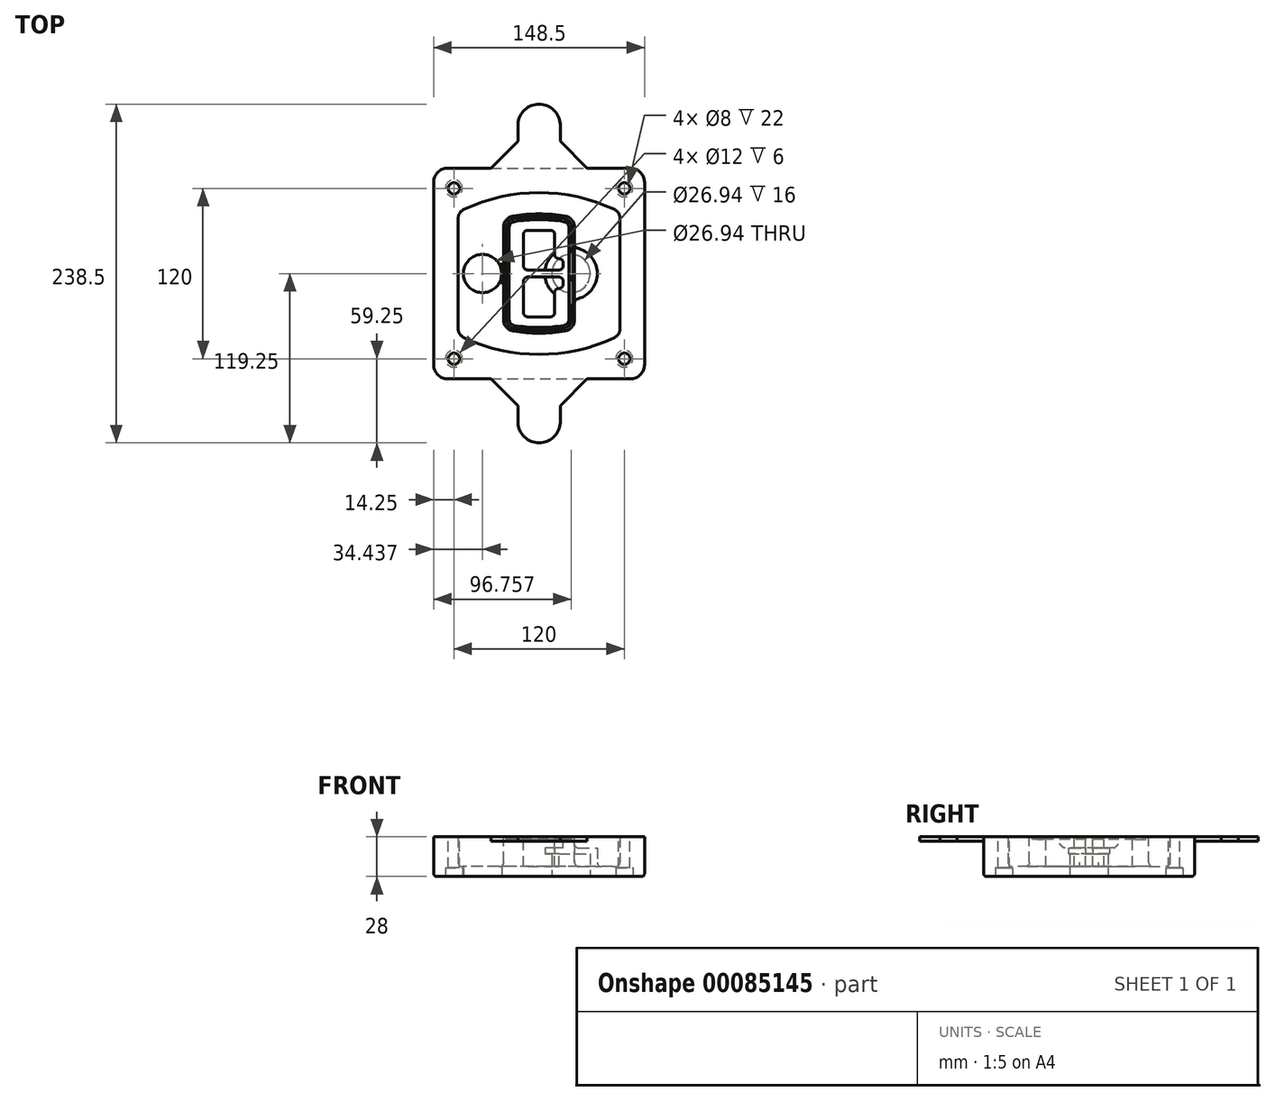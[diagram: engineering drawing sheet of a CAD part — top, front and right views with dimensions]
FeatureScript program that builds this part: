
annotation { "Feature Type Name" : "Feature", "Feature Type Description" : "" }
export const myFeature = defineFeature(function(context is Context, id is Id, definition is map)
    precondition{}
    {
        {
            var Q0;
            Q0=qCreatedBy(makeId("Top.planeOp"),FACE);
            var sketch = newSketch(context, id + "F0", { "sketchPlane" : qUnion([Q0])});
            skPoint(sketch, "E0.rect.middle", {"position": v(0, 0) * mm});
            skLineSegment(sketch, "E1.bottom", {"start": v(-64.25, -74.25) * mm, "end": v(64.25, -74.25) * mm});
            skLineSegment(sketch, "E1.top", {"start": v(-64.25, 74.25) * mm, "end": v(64.25, 74.25) * mm});
            skLineSegment(sketch, "E1.left", {"start": v(-74.25, -64.25) * mm, "end": v(-74.25, 64.25) * mm});
            skLineSegment(sketch, "E1.right", {"start": v(74.25, -64.25) * mm, "end": v(74.25, 64.25) * mm});
            skLineSegment(sketch, "E2", {"start": v(-74.25, 74.25) * mm, "end": v(74.25, -74.25) * mm, "construction": true});
            skLineSegment(sketch, "E3", {"start": v(74.25, 74.25) * mm, "end": v(-74.25, -74.25) * mm, "construction": true});
            skCircle(sketch, "E4", {"center": v(-60, 60) * mm, "radius": 4 * mm});
            skCircle(sketch, "E5", {"center": v(60, 60) * mm, "radius": 4 * mm});
            skCircle(sketch, "E6", {"center": v(60, -60) * mm, "radius": 4 * mm});
            skCircle(sketch, "E7", {"center": v(-60, -60) * mm, "radius": 4 * mm});
            skLineSegment(sketch, "E8", {"start": v(-60, 60) * mm, "end": v(60, 60) * mm, "construction": true});
            skLineSegment(sketch, "E9", {"start": v(60, 60) * mm, "end": v(60, -60) * mm, "construction": true});
            skLineSegment(sketch, "E10", {"start": v(60, -60) * mm, "end": v(-60, -60) * mm, "construction": true});
            skLineSegment(sketch, "E11", {"start": v(-60, -60) * mm, "end": v(-60, 60) * mm, "construction": true});
            skLineSegment(sketch, "E12", {"start": v(-60, 38.83) * mm, "end": v(-60, -38.83) * mm});
            skLineSegment(sketch, "E13", {"start": v(60, 38.83) * mm, "end": v(60, -38.83) * mm});
            skArc(sketch, "E14", {"start": v(54.26, 47.88) * mm, "mid": v(0, 60) * mm, "end": v(-54.26, 47.88) * mm});
            skArc(sketch, "E15", {"start": v(-54.26, -47.88) * mm, "mid": v(0, -60) * mm, "end": v(54.26, -47.88) * mm});
            skLineSegment(sketch, "E16", {"start": v(-60, 0) * mm, "end": v(60, 0) * mm, "construction": true});
            skPoint(sketch, "E17.visualSharp", {"position": v(-60, -45) * mm});
            skArc(sketch, "E17.filletArc", {"start": v(-60, -38.83) * mm, "mid": v(-58.44, -44.2) * mm, "end": v(-54.26, -47.88) * mm});
            skPoint(sketch, "E18.visualSharp", {"position": v(-60, 45) * mm});
            skArc(sketch, "E18.filletArc", {"start": v(-54.26, 47.88) * mm, "mid": v(-58.44, 44.2) * mm, "end": v(-60, 38.83) * mm});
            skPoint(sketch, "E19.visualSharp", {"position": v(60, 45) * mm});
            skArc(sketch, "E19.filletArc", {"start": v(60, 38.83) * mm, "mid": v(58.44, 44.2) * mm, "end": v(54.26, 47.88) * mm});
            skPoint(sketch, "E20.visualSharp", {"position": v(60, -45) * mm});
            skArc(sketch, "E20.filletArc", {"start": v(54.26, -47.88) * mm, "mid": v(58.44, -44.2) * mm, "end": v(60, -38.83) * mm});
            skPoint(sketch, "E21.visualSharp", {"position": v(-74.25, 74.25) * mm});
            skArc(sketch, "E21.filletArc", {"start": v(-64.25, 74.25) * mm, "mid": v(-71.32, 71.32) * mm, "end": v(-74.25, 64.25) * mm});
            skPoint(sketch, "E22.visualSharp", {"position": v(74.25, 74.25) * mm});
            skArc(sketch, "E22.filletArc", {"start": v(74.25, 64.25) * mm, "mid": v(71.32, 71.32) * mm, "end": v(64.25, 74.25) * mm});
            skPoint(sketch, "E23.visualSharp", {"position": v(74.25, -74.25) * mm});
            skArc(sketch, "E23.filletArc", {"start": v(64.25, -74.25) * mm, "mid": v(71.32, -71.32) * mm, "end": v(74.25, -64.25) * mm});
            skPoint(sketch, "E24.visualSharp", {"position": v(-74.25, -74.25) * mm});
            skArc(sketch, "E24.filletArc", {"start": v(-74.25, -64.25) * mm, "mid": v(-71.32, -71.32) * mm, "end": v(-64.25, -74.25) * mm});
            skArc(sketch, "E25.0", {"start": v(57, 38.83) * mm, "mid": v(55.9, 42.58) * mm, "end": v(52.98, 45.17) * mm});
            skLineSegment(sketch, "E25.1", {"start": v(57, 38.83) * mm, "end": v(57, -38.83) * mm});
            skArc(sketch, "E25.2", {"start": v(52.98, -45.17) * mm, "mid": v(55.9, -42.58) * mm, "end": v(57, -38.83) * mm});
            skArc(sketch, "E25.3", {"start": v(-52.98, -45.17) * mm, "mid": v(0, -57) * mm, "end": v(52.98, -45.17) * mm});
            skArc(sketch, "E25.4", {"start": v(-57, -38.83) * mm, "mid": v(-55.9, -42.58) * mm, "end": v(-52.98, -45.17) * mm});
            skArc(sketch, "E25.5", {"start": v(52.98, 45.17) * mm, "mid": v(0, 57) * mm, "end": v(-52.98, 45.17) * mm});
            skLineSegment(sketch, "E25.6", {"start": v(-57, 38.83) * mm, "end": v(-57, -38.83) * mm});
            skArc(sketch, "E25.7", {"start": v(-52.98, 45.17) * mm, "mid": v(-55.9, 42.58) * mm, "end": v(-57, 38.83) * mm});
            skArc(sketch, "E26.0", {"start": v(-55.96, 51.5) * mm, "mid": v(-61.82, 46.33) * mm, "end": v(-64, 38.83) * mm});
            skArc(sketch, "E26.1", {"start": v(55.96, 51.5) * mm, "mid": v(0, 64) * mm, "end": v(-55.96, 51.5) * mm});
            skArc(sketch, "E26.2", {"start": v(64, 38.83) * mm, "mid": v(61.82, 46.33) * mm, "end": v(55.96, 51.5) * mm});
            skLineSegment(sketch, "E26.3", {"start": v(64, 38.83) * mm, "end": v(64, -38.83) * mm});
            skArc(sketch, "E26.4", {"start": v(55.96, -51.5) * mm, "mid": v(61.82, -46.33) * mm, "end": v(64, -38.83) * mm});
            skLineSegment(sketch, "E26.5", {"start": v(-64, 38.83) * mm, "end": v(-64, -38.83) * mm});
            skArc(sketch, "E26.6", {"start": v(-55.96, -51.5) * mm, "mid": v(0, -64) * mm, "end": v(55.96, -51.5) * mm});
            skArc(sketch, "E26.7", {"start": v(-64, -38.83) * mm, "mid": v(-61.82, -46.33) * mm, "end": v(-55.96, -51.5) * mm});
            skSolve(sketch);
        }
        {
            var Q0;
            Q0=makeQuery(id+"F0.imprint","IMPRINT",FACE,{"disambiguationData":[TD([[makeQuery(id+"F0.imprint","IMPRINT",EDGE,{"derivedFrom":sQuery(id+"F0.wireOp",EDGE,"E1.bottom")}),1.0]])]});
            var Q1;
            Q1=makeQuery(id+"F0.imprint","IMPRINT",FACE,{"disambiguationData":[TD([[makeQuery(id+"F0.imprint","IMPRINT",EDGE,{"derivedFrom":sQuery(id+"F0.wireOp",EDGE,"E12")}),1.0]])]});
            var Q2;
            Q2=makeQuery(id+"F0.imprint","IMPRINT",FACE,{"disambiguationData":[TD([[makeQuery(id+"F0.imprint","IMPRINT",EDGE,{"derivedFrom":sQuery(id+"F0.wireOp",EDGE,"E25.0")}),1.0]])]});
            var Q3;
            Q3=makeQuery(id+"F0.imprint","IMPRINT",FACE,{"disambiguationData":[TD([[makeQuery(id+"F0.imprint","IMPRINT",EDGE,{"derivedFrom":sQuery(id+"F0.wireOp",EDGE,"E12")}),-1.0]])]});
            extrude(context, id + "F1", {"entities" : qUnion([Q0, Q1, Q2, Q3]), "oppositeDirection" : true, "depth" : 25 * mm});
        }
        {
            var Q0;
            Q0=makeQuery(id+"F0.imprint","IMPRINT",FACE,{"disambiguationData":[TD([[makeQuery(id+"F0.imprint","IMPRINT",EDGE,{"derivedFrom":sQuery(id+"F0.wireOp",EDGE,"E12")}),1.0]])]});
            extrude(context, id + "F2", {"entities" : qUnion([Q0]), "operationType" : NewBodyOperationType.ADD, "depth" : 3 * mm});
        }
        {
            var Q0;
            Q0=makeQuery(id+"F0.imprint","IMPRINT",FACE,{"disambiguationData":[TD([[makeQuery(id+"F0.imprint","IMPRINT",EDGE,{"derivedFrom":sQuery(id+"F0.wireOp",EDGE,"E25.0")}),1.0]])]});
            extrude(context, id + "F3", {"entities" : qUnion([Q0]), "operationType" : NewBodyOperationType.REMOVE, "oppositeDirection" : true, "depth" : 18 * mm});
        }
        {
            var Q0;
            Q0=makeQuery(id+"F2.opExtrude","CAP_FACE",FACE,{"disambiguationData":[OSD([sQuery(id+"F0.wireOp",EDGE,"E12"),sQuery(id+"F0.wireOp",EDGE,"E13"),sQuery(id+"F0.wireOp",EDGE,"E14"),sQuery(id+"F0.wireOp",EDGE,"E15"),sQuery(id+"F0.wireOp",EDGE,"E17.filletArc"),sQuery(id+"F0.wireOp",EDGE,"E18.filletArc"),sQuery(id+"F0.wireOp",EDGE,"E19.filletArc"),sQuery(id+"F0.wireOp",EDGE,"E20.filletArc"),sQuery(id+"F0.wireOp",EDGE,"E25.0"),sQuery(id+"F0.wireOp",EDGE,"E25.1"),sQuery(id+"F0.wireOp",EDGE,"E25.2"),sQuery(id+"F0.wireOp",EDGE,"E25.3"),sQuery(id+"F0.wireOp",EDGE,"E25.4"),sQuery(id+"F0.wireOp",EDGE,"E25.5"),sQuery(id+"F0.wireOp",EDGE,"E25.6"),sQuery(id+"F0.wireOp",EDGE,"E25.7")])],"isStart":false});
            var sketch = newSketch(context, id + "F4", { "sketchPlane" : qUnion([Q0])});
            skArc(sketch, "E27.0", {"start": v(-18.34, -40.45) * mm, "mid": v(0, -42) * mm, "end": v(18.34, -40.45) * mm});
            skArc(sketch, "E28.0", {"start": v(18.34, 40.45) * mm, "mid": v(0, 42) * mm, "end": v(-18.34, 40.45) * mm});
            skLineSegment(sketch, "E29", {"start": v(-25, 32.57) * mm, "end": v(-25, -32.57) * mm});
            skLineSegment(sketch, "E30", {"start": v(25, 32.57) * mm, "end": v(25, -32.57) * mm});
            skLineSegment(sketch, "E31", {"start": v(-25, 39.1) * mm, "end": v(25, 39.1) * mm, "construction": true});
            skLineSegment(sketch, "E32", {"start": v(-25, -39.1) * mm, "end": v(25, -39.1) * mm, "construction": true});
            skPoint(sketch, "E33.visualSharp", {"position": v(-25, 39.1) * mm});
            skArc(sketch, "E33.filletArc", {"start": v(-18.34, 40.45) * mm, "mid": v(-23.11, 37.73) * mm, "end": v(-25, 32.57) * mm});
            skPoint(sketch, "E34.visualSharp", {"position": v(25, 39.1) * mm});
            skArc(sketch, "E34.filletArc", {"start": v(25, 32.57) * mm, "mid": v(23.11, 37.73) * mm, "end": v(18.34, 40.45) * mm});
            skPoint(sketch, "E35.visualSharp", {"position": v(25, -39.1) * mm});
            skArc(sketch, "E35.filletArc", {"start": v(18.34, -40.45) * mm, "mid": v(23.11, -37.73) * mm, "end": v(25, -32.57) * mm});
            skPoint(sketch, "E36.visualSharp", {"position": v(-25, -39.1) * mm});
            skArc(sketch, "E36.filletArc", {"start": v(-25, -32.57) * mm, "mid": v(-23.11, -37.73) * mm, "end": v(-18.34, -40.45) * mm});
            skArc(sketch, "E37.0", {"start": v(52.98, 45.17) * mm, "mid": v(0, 57) * mm, "end": v(-52.98, 45.17) * mm});
            skArc(sketch, "E37.1", {"start": v(-52.98, 45.17) * mm, "mid": v(-55.9, 42.58) * mm, "end": v(-57, 38.83) * mm});
            skLineSegment(sketch, "E37.2", {"start": v(-57, 38.83) * mm, "end": v(-57, -38.83) * mm});
            skArc(sketch, "E37.3", {"start": v(-57, -38.83) * mm, "mid": v(-55.9, -42.58) * mm, "end": v(-52.98, -45.17) * mm});
            skArc(sketch, "E37.4", {"start": v(-52.98, -45.17) * mm, "mid": v(0, -57) * mm, "end": v(52.98, -45.17) * mm});
            skArc(sketch, "E37.5", {"start": v(52.98, -45.17) * mm, "mid": v(55.9, -42.58) * mm, "end": v(57, -38.83) * mm});
            skLineSegment(sketch, "E37.6", {"start": v(57, 38.83) * mm, "end": v(57, -38.83) * mm});
            skArc(sketch, "E37.7", {"start": v(57, 38.83) * mm, "mid": v(55.9, 42.58) * mm, "end": v(52.98, 45.17) * mm});
            skLineSegment(sketch, "E38.0", {"start": v(23, 32.57) * mm, "end": v(23, -32.57) * mm});
            skArc(sketch, "E38.1", {"start": v(18, -38.48) * mm, "mid": v(21.58, -36.44) * mm, "end": v(23, -32.57) * mm});
            skArc(sketch, "E38.2", {"start": v(-18, -38.48) * mm, "mid": v(0, -40) * mm, "end": v(18, -38.48) * mm});
            skArc(sketch, "E38.3", {"start": v(-23, -32.57) * mm, "mid": v(-21.58, -36.44) * mm, "end": v(-18, -38.48) * mm});
            skLineSegment(sketch, "E38.4", {"start": v(-23, 32.57) * mm, "end": v(-23, -32.57) * mm});
            skArc(sketch, "E38.5", {"start": v(23, 32.57) * mm, "mid": v(21.58, 36.44) * mm, "end": v(18, 38.48) * mm});
            skArc(sketch, "E38.6", {"start": v(-18, 38.48) * mm, "mid": v(-21.58, 36.44) * mm, "end": v(-23, 32.57) * mm});
            skArc(sketch, "E38.7", {"start": v(18, 38.48) * mm, "mid": v(0, 40) * mm, "end": v(-18, 38.48) * mm});
            skArc(sketch, "E39.0", {"start": v(21, 32.57) * mm, "mid": v(20.06, 35.15) * mm, "end": v(17.67, 36.5) * mm});
            skLineSegment(sketch, "E39.1", {"start": v(21, 32.57) * mm, "end": v(21, -32.57) * mm});
            skArc(sketch, "E39.2", {"start": v(17.67, -36.5) * mm, "mid": v(20.06, -35.15) * mm, "end": v(21, -32.57) * mm});
            skArc(sketch, "E39.3", {"start": v(-17.67, -36.5) * mm, "mid": v(0, -38) * mm, "end": v(17.67, -36.5) * mm});
            skArc(sketch, "E39.4", {"start": v(-21, -32.57) * mm, "mid": v(-20.06, -35.15) * mm, "end": v(-17.67, -36.5) * mm});
            skArc(sketch, "E39.5", {"start": v(17.67, 36.5) * mm, "mid": v(0, 38) * mm, "end": v(-17.67, 36.5) * mm});
            skLineSegment(sketch, "E39.6", {"start": v(-21, 32.57) * mm, "end": v(-21, -32.57) * mm});
            skArc(sketch, "E39.7", {"start": v(-17.67, 36.5) * mm, "mid": v(-20.06, 35.15) * mm, "end": v(-21, 32.57) * mm});
            skLineSegment(sketch, "E40", {"start": v(-25, 0) * mm, "end": v(25, 0) * mm, "construction": true});
            skLineSegment(sketch, "E41", {"start": v(-11, 5.5) * mm, "end": v(-11, 27.5) * mm});
            skLineSegment(sketch, "E42", {"start": v(-8, 30.5) * mm, "end": v(8, 30.5) * mm});
            skLineSegment(sketch, "E43", {"start": v(11, 27.5) * mm, "end": v(11, 13.5) * mm});
            skLineSegment(sketch, "E44", {"start": v(14, 10.5) * mm, "end": v(14, 10.5) * mm});
            skLineSegment(sketch, "E45", {"start": v(17, 7.5) * mm, "end": v(17, 5.5) * mm});
            skLineSegment(sketch, "E46", {"start": v(14, 2.5) * mm, "end": v(-8, 2.5) * mm});
            skPoint(sketch, "E47.visualSharp", {"position": v(-11, 30.5) * mm});
            skArc(sketch, "E47.filletArc", {"start": v(-8, 30.5) * mm, "mid": v(-10.12, 29.62) * mm, "end": v(-11, 27.5) * mm});
            skPoint(sketch, "E48.visualSharp", {"position": v(11, 30.5) * mm});
            skArc(sketch, "E48.filletArc", {"start": v(11, 27.5) * mm, "mid": v(10.12, 29.62) * mm, "end": v(8, 30.5) * mm});
            skPoint(sketch, "E49.visualSharp", {"position": v(11, 10.5) * mm});
            skArc(sketch, "E49.filletArc", {"start": v(11, 13.5) * mm, "mid": v(11.88, 11.38) * mm, "end": v(14, 10.5) * mm});
            skPoint(sketch, "E50.visualSharp", {"position": v(17, 10.5) * mm});
            skArc(sketch, "E50.filletArc", {"start": v(17, 7.5) * mm, "mid": v(16.12, 9.62) * mm, "end": v(14, 10.5) * mm});
            skPoint(sketch, "E51.visualSharp", {"position": v(17, 2.5) * mm});
            skArc(sketch, "E51.filletArc", {"start": v(14, 2.5) * mm, "mid": v(16.12, 3.38) * mm, "end": v(17, 5.5) * mm});
            skPoint(sketch, "E52.visualSharp", {"position": v(-11, 2.5) * mm});
            skArc(sketch, "E52.filletArc", {"start": v(-11, 5.5) * mm, "mid": v(-10.12, 3.38) * mm, "end": v(-8, 2.5) * mm});
            skLineSegment(sketch, "E53.0.MirrorCS", {"start": v(14, -2.5) * mm, "end": v(-8, -2.5) * mm});
            skArc(sketch, "E54.0.MirrorCS", {"start": v(-11, -5.5) * mm, "mid": v(-10.12, -3.38) * mm, "end": v(-8, -2.5) * mm});
            skLineSegment(sketch, "E55.0.MirrorCS", {"start": v(-11, -5.5) * mm, "end": v(-11, -27.5) * mm});
            skArc(sketch, "E56.0.MirrorCS", {"start": v(-8, -30.5) * mm, "mid": v(-10.12, -29.62) * mm, "end": v(-11, -27.5) * mm});
            skLineSegment(sketch, "E57.0.MirrorCS", {"start": v(-8, -30.5) * mm, "end": v(8, -30.5) * mm});
            skArc(sketch, "E58.0.MirrorCS", {"start": v(11, -27.5) * mm, "mid": v(10.12, -29.62) * mm, "end": v(8, -30.5) * mm});
            skLineSegment(sketch, "E59.0.MirrorCS", {"start": v(11, -27.5) * mm, "end": v(11, -13.5) * mm});
            skArc(sketch, "E60.0.MirrorCS", {"start": v(11, -13.5) * mm, "mid": v(11.88, -11.38) * mm, "end": v(14, -10.5) * mm});
            skArc(sketch, "E61.0.MirrorCS", {"start": v(17, -7.5) * mm, "mid": v(16.12, -9.62) * mm, "end": v(14, -10.5) * mm});
            skLineSegment(sketch, "E62.0.MirrorCS", {"start": v(17, -7.5) * mm, "end": v(17, -5.5) * mm});
            skArc(sketch, "E63.0.MirrorCS", {"start": v(14, -2.5) * mm, "mid": v(16.12, -3.38) * mm, "end": v(17, -5.5) * mm});
            skSolve(sketch);
        }
        {
            var Q0;
            Q0=makeQuery(id+"F4.imprint","IMPRINT",FACE,{"disambiguationData":[TD([[makeQuery(id+"F4.imprint","IMPRINT",EDGE,{"derivedFrom":sQuery(id+"F4.wireOp",EDGE,"E27.0")}),1.0]])]});
            var Q1;
            Q1=makeQuery(id+"F4.imprint","IMPRINT",FACE,{"disambiguationData":[TD([[makeQuery(id+"F4.imprint","IMPRINT",EDGE,{"derivedFrom":sQuery(id+"F4.wireOp",EDGE,"E38.0")}),-1.0]])]});
            var Q2;
            Q2=makeQuery(id+"F4.imprint","IMPRINT",FACE,{"disambiguationData":[TD([[makeQuery(id+"F4.imprint","IMPRINT",EDGE,{"derivedFrom":sQuery(id+"F4.wireOp",EDGE,"E39.0")}),1.0]])]});
            extrude(context, id + "F5", {"entities" : qUnion([Q0, Q1, Q2]), "operationType" : NewBodyOperationType.ADD, "endBound" : BoundingType.UP_TO_NEXT, "oppositeDirection" : true, "depth" : 25 * mm});
        }
        {
            var Q0;
            Q0=makeQuery(id+"F4.imprint","IMPRINT",FACE,{"disambiguationData":[TD([[makeQuery(id+"F4.imprint","IMPRINT",EDGE,{"derivedFrom":sQuery(id+"F4.wireOp",EDGE,"E38.0")}),-1.0]])]});
            extrude(context, id + "F6", {"entities" : qUnion([Q0]), "operationType" : NewBodyOperationType.REMOVE, "oppositeDirection" : true, "depth" : 2 * mm});
        }
        {
            var Q0;
            Q0=makeQuery(id+"F1.opExtrude","CAP_FACE",FACE,{"disambiguationData":[OSD([sQuery(id+"F0.wireOp",EDGE,"E1.bottom"),sQuery(id+"F0.wireOp",EDGE,"E1.top"),sQuery(id+"F0.wireOp",EDGE,"E1.left"),sQuery(id+"F0.wireOp",EDGE,"E1.right"),sQuery(id+"F0.wireOp",EDGE,"E4"),sQuery(id+"F0.wireOp",EDGE,"E5"),sQuery(id+"F0.wireOp",EDGE,"E6"),sQuery(id+"F0.wireOp",EDGE,"E7"),sQuery(id+"F0.wireOp",EDGE,"E21.filletArc"),sQuery(id+"F0.wireOp",EDGE,"E22.filletArc"),sQuery(id+"F0.wireOp",EDGE,"E23.filletArc"),sQuery(id+"F0.wireOp",EDGE,"E24.filletArc")])],"isStart":false});
            var sketch = newSketch(context, id + "F7", { "sketchPlane" : qUnion([Q0])});
            skCircle(sketch, "E64", {"center": v(22.5, 0) * mm, "radius": 13.47 * mm});
            skCircle(sketch, "E65", {"center": v(-39.81, 0) * mm, "radius": 13.47 * mm});
            skLineSegment(sketch, "E66", {"start": v(74.25, 0) * mm, "end": v(-74.25, 0) * mm});
            skCircle(sketch, "E67", {"center": v(22.5, 0) * mm, "radius": 18.47 * mm});
            skCircle(sketch, "E68", {"center": v(60, -60) * mm, "radius": 6 * mm});
            skCircle(sketch, "E69", {"center": v(-60, -60) * mm, "radius": 6 * mm});
            skCircle(sketch, "E70", {"center": v(-60, 60) * mm, "radius": 6 * mm});
            skCircle(sketch, "E71", {"center": v(60, 60) * mm, "radius": 6 * mm});
            skSolve(sketch);
        }
        {
            var Q0;
            {var subQ1=sQuery(id+"F7.wireOp",EDGE,"E66");var subQ4=sQuery(id+"F7.wireOp",EDGE,"E64");var subQ6=makeQuery(id+"F7.imprint","INTERSECT",VERTEX,{"disambiguationData":[OD(0.0)],"derivedFrom":[subQ4,subQ1]});Q0=makeQuery(id+"F7.imprint","IMPRINT",FACE,{"disambiguationData":[TD([[makeQuery(id+"F7.imprint","IMPRINT",EDGE,{"disambiguationData":[TD([[subQ6,-1.0]])],"derivedFrom":subQ4}),-1.0]])]});}
            var Q1;
            {var subQ0=sQuery(id+"F7.wireOp",EDGE,"E66");var subQ1=sQuery(id+"F7.wireOp",EDGE,"E64");var subQ3=makeQuery(id+"F7.imprint","INTERSECT",VERTEX,{"disambiguationData":[OD(0.0)],"derivedFrom":[subQ1,subQ0]});Q1=makeQuery(id+"F7.imprint","IMPRINT",FACE,{"disambiguationData":[TD([[makeQuery(id+"F7.imprint","IMPRINT",EDGE,{"disambiguationData":[TD([[subQ3,-1.0]])],"derivedFrom":subQ1}),1.0]])]});}
            var Q2;
            {var subQ0=sQuery(id+"F7.wireOp",EDGE,"E66");var subQ1=sQuery(id+"F7.wireOp",EDGE,"E64");var subQ3=makeQuery(id+"F7.imprint","INTERSECT",VERTEX,{"disambiguationData":[OD(0.0)],"derivedFrom":[subQ1,subQ0]});Q2=makeQuery(id+"F7.imprint","IMPRINT",FACE,{"disambiguationData":[TD([[makeQuery(id+"F7.imprint","IMPRINT",EDGE,{"disambiguationData":[TD([[subQ3,1.0]])],"derivedFrom":subQ1}),1.0]])]});}
            var Q3;
            {var subQ1=sQuery(id+"F7.wireOp",EDGE,"E66");var subQ4=sQuery(id+"F7.wireOp",EDGE,"E64");var subQ6=makeQuery(id+"F7.imprint","INTERSECT",VERTEX,{"disambiguationData":[OD(0.0)],"derivedFrom":[subQ4,subQ1]});Q3=makeQuery(id+"F7.imprint","IMPRINT",FACE,{"disambiguationData":[TD([[makeQuery(id+"F7.imprint","IMPRINT",EDGE,{"disambiguationData":[TD([[subQ6,1.0]])],"derivedFrom":subQ4}),-1.0]])]});}
            extrude(context, id + "F8", {"entities" : qUnion([Q0, Q1, Q2, Q3]), "operationType" : NewBodyOperationType.ADD, "oppositeDirection" : true, "depth" : 20 * mm});
        }
        {
            var Q0;
            {var subQ0=sQuery(id+"F7.wireOp",EDGE,"E66");var subQ1=sQuery(id+"F7.wireOp",EDGE,"E64");var subQ3=makeQuery(id+"F7.imprint","INTERSECT",VERTEX,{"disambiguationData":[OD(0.0)],"derivedFrom":[subQ1,subQ0]});Q0=makeQuery(id+"F7.imprint","IMPRINT",FACE,{"disambiguationData":[TD([[makeQuery(id+"F7.imprint","IMPRINT",EDGE,{"disambiguationData":[TD([[subQ3,-1.0]])],"derivedFrom":subQ1}),1.0]])]});}
            var Q1;
            {var subQ0=sQuery(id+"F7.wireOp",EDGE,"E66");var subQ1=sQuery(id+"F7.wireOp",EDGE,"E64");var subQ3=makeQuery(id+"F7.imprint","INTERSECT",VERTEX,{"disambiguationData":[OD(0.0)],"derivedFrom":[subQ1,subQ0]});Q1=makeQuery(id+"F7.imprint","IMPRINT",FACE,{"disambiguationData":[TD([[makeQuery(id+"F7.imprint","IMPRINT",EDGE,{"disambiguationData":[TD([[subQ3,1.0]])],"derivedFrom":subQ1}),1.0]])]});}
            extrude(context, id + "F9", {"entities" : qUnion([Q0, Q1]), "operationType" : NewBodyOperationType.REMOVE, "oppositeDirection" : true, "depth" : 16 * mm});
        }
        {
            var Q0;
            {var subQ0=sQuery(id+"F7.wireOp",EDGE,"E66");var subQ1=sQuery(id+"F7.wireOp",EDGE,"E65");var subQ3=makeQuery(id+"F7.imprint","INTERSECT",VERTEX,{"disambiguationData":[OD(0.0)],"derivedFrom":[subQ1,subQ0]});Q0=makeQuery(id+"F7.imprint","IMPRINT",FACE,{"disambiguationData":[TD([[makeQuery(id+"F7.imprint","IMPRINT",EDGE,{"disambiguationData":[TD([[subQ3,-1.0]])],"derivedFrom":subQ1}),1.0]])]});}
            var Q1;
            {var subQ0=sQuery(id+"F7.wireOp",EDGE,"E66");var subQ1=sQuery(id+"F7.wireOp",EDGE,"E65");var subQ3=makeQuery(id+"F7.imprint","INTERSECT",VERTEX,{"disambiguationData":[OD(0.0)],"derivedFrom":[subQ1,subQ0]});Q1=makeQuery(id+"F7.imprint","IMPRINT",FACE,{"disambiguationData":[TD([[makeQuery(id+"F7.imprint","IMPRINT",EDGE,{"disambiguationData":[TD([[subQ3,1.0]])],"derivedFrom":subQ1}),1.0]])]});}
            extrude(context, id + "F10", {"entities" : qUnion([Q0, Q1]), "operationType" : NewBodyOperationType.REMOVE, "oppositeDirection" : true, "depth" : 25 * mm});
        }
        {
            var Q0;
            Q0=makeQuery(id+"F7.imprint","IMPRINT",FACE,{"disambiguationData":[TD([[makeQuery(id+"F7.imprint","IMPRINT",EDGE,{"derivedFrom":sQuery(id+"F7.wireOp",EDGE,"E68")}),1.0]])]});
            var Q1;
            Q1=makeQuery(id+"F7.imprint","IMPRINT",FACE,{"disambiguationData":[TD([[makeQuery(id+"F7.imprint","IMPRINT",EDGE,{"derivedFrom":makeQuery(id+"F1.opExtrude","CAP_EDGE",EDGE,{"disambiguationData":[OSD([sQuery(id+"F0.wireOp",EDGE,"E5")])],"isStart":false})}),-1.0]])]});
            var Q2;
            Q2=makeQuery(id+"F7.imprint","IMPRINT",FACE,{"disambiguationData":[TD([[makeQuery(id+"F7.imprint","IMPRINT",EDGE,{"derivedFrom":sQuery(id+"F7.wireOp",EDGE,"E69")}),1.0]])]});
            var Q3;
            Q3=makeQuery(id+"F7.imprint","IMPRINT",FACE,{"disambiguationData":[TD([[makeQuery(id+"F7.imprint","IMPRINT",EDGE,{"derivedFrom":makeQuery(id+"F1.opExtrude","CAP_EDGE",EDGE,{"disambiguationData":[OSD([sQuery(id+"F0.wireOp",EDGE,"E4")])],"isStart":false})}),-1.0]])]});
            var Q4;
            Q4=makeQuery(id+"F7.imprint","IMPRINT",FACE,{"disambiguationData":[TD([[makeQuery(id+"F7.imprint","IMPRINT",EDGE,{"derivedFrom":sQuery(id+"F7.wireOp",EDGE,"E70")}),1.0]])]});
            var Q5;
            Q5=makeQuery(id+"F7.imprint","IMPRINT",FACE,{"disambiguationData":[TD([[makeQuery(id+"F7.imprint","IMPRINT",EDGE,{"derivedFrom":makeQuery(id+"F1.opExtrude","CAP_EDGE",EDGE,{"disambiguationData":[OSD([sQuery(id+"F0.wireOp",EDGE,"E7")])],"isStart":false})}),-1.0]])]});
            var Q6;
            Q6=makeQuery(id+"F7.imprint","IMPRINT",FACE,{"disambiguationData":[TD([[makeQuery(id+"F7.imprint","IMPRINT",EDGE,{"derivedFrom":sQuery(id+"F7.wireOp",EDGE,"E71")}),1.0]])]});
            var Q7;
            Q7=makeQuery(id+"F7.imprint","IMPRINT",FACE,{"disambiguationData":[TD([[makeQuery(id+"F7.imprint","IMPRINT",EDGE,{"derivedFrom":makeQuery(id+"F1.opExtrude","CAP_EDGE",EDGE,{"disambiguationData":[OSD([sQuery(id+"F0.wireOp",EDGE,"E6")])],"isStart":false})}),-1.0]])]});
            extrude(context, id + "F11", {"entities" : qUnion([Q0, Q1, Q2, Q3, Q4, Q5, Q6, Q7]), "operationType" : NewBodyOperationType.REMOVE, "oppositeDirection" : true, "depth" : 6 * mm});
        }
        {
            var Q0;
            Q0=makeQuery(id+"F9.boolean.opBoolean","COPY",FACE,{"derivedFrom":makeQuery(id+"F9.opExtrude","CAP_FACE",FACE,{"disambiguationData":[OSD([sQuery(id+"F7.wireOp",EDGE,"E64")])],"isStart":false})});
            var sketch = newSketch(context, id + "F12", { "sketchPlane" : qUnion([Q0])});
            skArc(sketch, "E72.0", {"start": v(11, 14.45) * mm, "mid": v(6.45, 9.13) * mm, "end": v(4.2, 2.5) * mm});
            skArc(sketch, "E72.1", {"start": v(4.2, -2.5) * mm, "mid": v(6.45, -9.13) * mm, "end": v(11, -14.45) * mm});
            skLineSegment(sketch, "E73", {"start": v(4.2, -2.5) * mm, "end": v(14, -2.5) * mm});
            skLineSegment(sketch, "E74.0", {"start": v(14, 2.5) * mm, "end": v(4.2, 2.5) * mm});
            skArc(sketch, "E74.1", {"start": v(14, 2.5) * mm, "mid": v(16.12, 3.38) * mm, "end": v(17, 5.5) * mm});
            skLineSegment(sketch, "E74.2", {"start": v(17, 7.5) * mm, "end": v(17, 5.5) * mm});
            skArc(sketch, "E74.3", {"start": v(17, 7.5) * mm, "mid": v(16.12, 9.62) * mm, "end": v(14, 10.5) * mm});
            skArc(sketch, "E74.4", {"start": v(11, 13.5) * mm, "mid": v(11.88, 11.38) * mm, "end": v(14, 10.5) * mm});
            skLineSegment(sketch, "E74.5", {"start": v(11, 14.45) * mm, "end": v(11, 13.5) * mm});
            skLineSegment(sketch, "E74.7", {"start": v(14, -2.5) * mm, "end": v(4.2, -2.5) * mm});
            skArc(sketch, "E74.8", {"start": v(14, -2.5) * mm, "mid": v(16.12, -3.38) * mm, "end": v(17, -5.5) * mm});
            skLineSegment(sketch, "E74.9", {"start": v(17, -7.5) * mm, "end": v(17, -5.5) * mm});
            skArc(sketch, "E74.10", {"start": v(17, -7.5) * mm, "mid": v(16.12, -9.62) * mm, "end": v(14, -10.5) * mm});
            skArc(sketch, "E74.11", {"start": v(11, -13.5) * mm, "mid": v(11.88, -11.38) * mm, "end": v(14, -10.5) * mm});
            skLineSegment(sketch, "E74.12", {"start": v(11, -14.45) * mm, "end": v(11, -13.5) * mm});
            skPoint(sketch, "E75.orphan", {"position": v(11, -27.5) * mm});
            skPoint(sketch, "E76.orphan", {"position": v(-8, -2.5) * mm});
            skPoint(sketch, "E77.orphan", {"position": v(-8, 2.5) * mm});
            skPoint(sketch, "E78.orphan", {"position": v(11, 27.5) * mm});
            skSolve(sketch);
        }
        {
            var Q0;
            {var subQ7=sQuery(id+"F12.wireOp",EDGE,"E72.0");var subQ14=sQuery(id+"F12.wireOp",EDGE,"E72.1");var subQ16=sQuery(id+"F12.wireOp",EDGE,"E74.1");var subQ18=sQuery(id+"F12.wireOp",EDGE,"E74.8");Q0=qUnion([makeQuery(id+"F12.imprint","IMPRINT",FACE,{"disambiguationData":[TD([[makeQuery(id+"F12.imprint","IMPRINT",EDGE,{"derivedFrom":subQ7}),1.0]])]}),makeQuery(id+"F12.imprint","IMPRINT",FACE,{"disambiguationData":[TD([[makeQuery(id+"F12.imprint","IMPRINT",EDGE,{"derivedFrom":subQ14}),1.0]])]}),makeQuery(id+"F12.imprint","IMPRINT",FACE,{"disambiguationData":[TD([[makeQuery(id+"F12.imprint","IMPRINT",EDGE,{"derivedFrom":subQ16}),1.0]])]}),makeQuery(id+"F12.imprint","IMPRINT",FACE,{"disambiguationData":[TD([[makeQuery(id+"F12.imprint","IMPRINT",EDGE,{"derivedFrom":subQ18}),-1.0]])]})]);}
            var Q1;
            Q1=makeQuery(id+"F5.boolean.opBoolean","SPLIT",FACE,{"disambiguationData":[TD([makeQuery(id+"F5.opExtrude","SWEPT_FACE",FACE,{"disambiguationData":[OSD([sQuery(id+"F4.wireOp",EDGE,"E41")])]})])],"derivedFrom":makeQuery(id+"F3.boolean.opBoolean","COPY",FACE,{"derivedFrom":makeQuery(id+"F3.opExtrude","CAP_FACE",FACE,{"disambiguationData":[OSD([sQuery(id+"F0.wireOp",EDGE,"E25.0"),sQuery(id+"F0.wireOp",EDGE,"E25.1"),sQuery(id+"F0.wireOp",EDGE,"E25.2"),sQuery(id+"F0.wireOp",EDGE,"E25.3"),sQuery(id+"F0.wireOp",EDGE,"E25.4"),sQuery(id+"F0.wireOp",EDGE,"E25.5"),sQuery(id+"F0.wireOp",EDGE,"E25.6"),sQuery(id+"F0.wireOp",EDGE,"E25.7")])],"isStart":false})})});
            extrude(context, id + "F13", {"entities" : qUnion([Q0]), "operationType" : NewBodyOperationType.REMOVE, "endBound" : BoundingType.UP_TO_SURFACE, "endBoundEntityFace" : qUnion([Q1]), "depth" : 25 * mm});
        }
        {
            var Q0;
            Q0=makeQuery(id+"F3.boolean.opBoolean","COPY",EDGE,{"derivedFrom":makeQuery(id+"F3.opExtrude","CAP_EDGE",EDGE,{"disambiguationData":[OSD([sQuery(id+"F0.wireOp",EDGE,"E25.6")])],"isStart":false})});
            var Q1;
            Q1=makeQuery(id+"F8.boolean.opBoolean","INTERSECT",EDGE,{"derivedFrom":[makeQuery(id+"F5.opExtrude","SWEPT_FACE",FACE,{"disambiguationData":[OSD([sQuery(id+"F4.wireOp",EDGE,"E30")])]}),makeQuery(id+"F8.opExtrude","CAP_FACE",FACE,{"disambiguationData":[OSD([sQuery(id+"F7.wireOp",EDGE,"E67")])],"isStart":false})]});
            var Q2;
            Q2=makeQuery(id+"F8.boolean.opBoolean","INTERSECT",EDGE,{"disambiguationData":[OD(1.0)],"derivedFrom":[makeQuery(id+"F5.opExtrude","SWEPT_FACE",FACE,{"disambiguationData":[OSD([sQuery(id+"F4.wireOp",EDGE,"E30")])]}),makeQuery(id+"F8.opExtrude","SWEPT_FACE",FACE,{"disambiguationData":[OSD([sQuery(id+"F7.wireOp",EDGE,"E67")])]})]});
            var Q3;
            {var subQ0=sQuery(id+"F4.wireOp",EDGE,"E30");Q3=makeQuery(id+"F8.boolean.opBoolean","SPLIT",EDGE,{"disambiguationData":[TD([makeQuery(id+"F5.opExtrude","SWEPT_FACE",FACE,{"disambiguationData":[OSD([sQuery(id+"F4.wireOp",EDGE,"E35.filletArc")])]})])],"derivedFrom":makeQuery(id+"F5.opExtrude","CAP_EDGE",EDGE,{"disambiguationData":[OSD([subQ0])],"isStart":false})});}
            var Q4;
            {var subQ0=sQuery(id+"F0.wireOp",EDGE,"E25.7");var subQ1=sQuery(id+"F0.wireOp",EDGE,"E25.1");var subQ2=sQuery(id+"F0.wireOp",EDGE,"E25.6");var subQ3=sQuery(id+"F0.wireOp",EDGE,"E25.5");var subQ4=sQuery(id+"F0.wireOp",EDGE,"E25.4");var subQ5=sQuery(id+"F0.wireOp",EDGE,"E25.0");var subQ6=sQuery(id+"F0.wireOp",EDGE,"E25.2");var subQ7=sQuery(id+"F0.wireOp",EDGE,"E25.3");Q4=makeQuery(id+"F8.boolean.opBoolean","INTERSECT",EDGE,{"derivedFrom":[makeQuery(id+"F5.boolean.opBoolean","SPLIT",FACE,{"disambiguationData":[TD([makeQuery(id+"F2.opExtrude","SWEPT_FACE",FACE,{"disambiguationData":[OSD([subQ5])]})])],"derivedFrom":makeQuery(id+"F3.boolean.opBoolean","COPY",FACE,{"derivedFrom":makeQuery(id+"F3.opExtrude","CAP_FACE",FACE,{"disambiguationData":[OSD([subQ5,subQ1,subQ6,subQ7,subQ4,subQ3,subQ2,subQ0])],"isStart":false})})}),makeQuery(id+"F8.opExtrude","SWEPT_FACE",FACE,{"disambiguationData":[OSD([sQuery(id+"F7.wireOp",EDGE,"E67")])]})]});}
            var Q5;
            Q5=makeQuery(id+"F8.boolean.opBoolean","INTERSECT",EDGE,{"disambiguationData":[OD(0.0)],"derivedFrom":[makeQuery(id+"F5.opExtrude","SWEPT_FACE",FACE,{"disambiguationData":[OSD([sQuery(id+"F4.wireOp",EDGE,"E30")])]}),makeQuery(id+"F8.opExtrude","SWEPT_FACE",FACE,{"disambiguationData":[OSD([sQuery(id+"F7.wireOp",EDGE,"E67")])]})]});
            fillet(context, id + "F14", {"entities" : qUnion([Q0, Q1, Q2, Q3, Q4, Q5]), "radius" : 3 * mm, "tangentPropagation" : true, "allowEdgeOverflow" : false});
        }
        {
            var Q0;
            Q0=makeQuery(id+"F1.opExtrude","CAP_EDGE",EDGE,{"disambiguationData":[OSD([sQuery(id+"F0.wireOp",EDGE,"E1.bottom")])],"isStart":false});
            fillet(context, id + "F15", {"entities" : qUnion([Q0]), "radius" : 2 * mm, "tangentPropagation" : true, "allowEdgeOverflow" : false});
        }
        {
            var Q0;
            {var subQ0=sQuery(id+"F0.wireOp",EDGE,"E22.filletArc");var subQ1=sQuery(id+"F0.wireOp",EDGE,"E7");var subQ2=sQuery(id+"F0.wireOp",EDGE,"E6");var subQ3=sQuery(id+"F0.wireOp",EDGE,"E5");var subQ4=sQuery(id+"F0.wireOp",EDGE,"E4");var subQ5=sQuery(id+"F0.wireOp",EDGE,"E1.bottom");var subQ6=sQuery(id+"F0.wireOp",EDGE,"E21.filletArc");var subQ7=sQuery(id+"F0.wireOp",EDGE,"E1.top");var subQ8=sQuery(id+"F0.wireOp",EDGE,"E1.left");var subQ9=sQuery(id+"F0.wireOp",EDGE,"E1.right");var subQ10=sQuery(id+"F0.wireOp",EDGE,"E23.filletArc");var subQ11=sQuery(id+"F0.wireOp",EDGE,"E24.filletArc");Q0=makeQuery(id+"F2.boolean.opBoolean","SPLIT",FACE,{"disambiguationData":[TD([makeQuery(id+"F1.opExtrude","SWEPT_FACE",FACE,{"disambiguationData":[OSD([subQ5])]})])],"derivedFrom":makeQuery(id+"F1.opExtrude","CAP_FACE",FACE,{"disambiguationData":[OSD([subQ5,subQ7,subQ8,subQ9,subQ4,subQ3,subQ2,subQ1,subQ6,subQ0,subQ10,subQ11])],"isStart":true})});}
            var sketch = newSketch(context, id + "F16", { "sketchPlane" : qUnion([Q0])});
            skLineSegment(sketch, "E79", {"start": v(0, 74.25) * mm, "end": v(0, 104.25) * mm, "construction": true});
            skCircle(sketch, "E80", {"center": v(0, 104.25) * mm, "radius": 6 * mm});
            skArc(sketch, "E81", {"start": v(14.98, 105.1) * mm, "mid": v(0.03, 119.25) * mm, "end": v(-14.97, 105.17) * mm});
            skLineSegment(sketch, "E82", {"start": v(-14.97, 105.17) * mm, "end": v(-14.97, 93.17) * mm});
            skLineSegment(sketch, "E83", {"start": v(14.98, 105.1) * mm, "end": v(14.98, 93.1) * mm});
            skLineSegment(sketch, "E84", {"start": v(-14.97, 93.17) * mm, "end": v(-33.9, 74.25) * mm});
            skLineSegment(sketch, "E85", {"start": v(14.98, 93.1) * mm, "end": v(33.83, 74.25) * mm});
            skLineSegment(sketch, "E86", {"start": v(-74.25, 0) * mm, "end": v(74.25, 0) * mm, "construction": true});
            skLineSegment(sketch, "E87.MirrorCS", {"start": v(14.98, -93.1) * mm, "end": v(33.83, -74.25) * mm});
            skLineSegment(sketch, "E88.MirrorCS", {"start": v(14.98, -105.1) * mm, "end": v(14.98, -93.1) * mm});
            skArc(sketch, "E89.MirrorCS", {"start": v(14.98, -105.1) * mm, "mid": v(0.03, -119.25) * mm, "end": v(-14.97, -105.17) * mm});
            skLineSegment(sketch, "E90.MirrorCS", {"start": v(-14.97, -105.17) * mm, "end": v(-14.97, -93.17) * mm});
            skLineSegment(sketch, "E91.MirrorCS", {"start": v(-14.97, -93.17) * mm, "end": v(-33.9, -74.25) * mm});
            skLineSegment(sketch, "E92.MirrorCS", {"start": v(0, -74.25) * mm, "end": v(0, -104.25) * mm, "construction": true});
            skCircle(sketch, "E93.MirrorC", {"center": v(0, -104.25) * mm, "radius": 6 * mm});
            skSolve(sketch);
        }
        {
            var Q0;
            Q0 = qSketchRegion(id + "F16", true);
            var Q1;
            Q1=makeQuery(id+"F16.imprint","IMPRINT",FACE,{"disambiguationData":[TD([[makeQuery(id+"F16.imprint","IMPRINT",EDGE,{"derivedFrom":sQuery(id+"F16.wireOp",EDGE,"E80")}),-1.0]])]});
            var Q2;
            Q2=makeQuery(id+"F16.imprint","IMPRINT",FACE,{"disambiguationData":[TD([[makeQuery(id+"F16.imprint","IMPRINT",EDGE,{"derivedFrom":makeQuery(id+"F1.opExtrude","CAP_EDGE",EDGE,{"disambiguationData":[OSD([sQuery(id+"F0.wireOp",EDGE,"E1.left")])],"isStart":true})}),-1.0]])]});
            var Q3;
            {var subQ0=sQuery(id+"F16.wireOp",EDGE,"E87.MirrorCS");Q3=makeQuery(id+"F16.imprint","IMPRINT",FACE,{"disambiguationData":[TD([[makeQuery(id+"F16.imprint","IMPRINT",EDGE,{"derivedFrom":subQ0}),1.0]])]});}
            var Q4;
            Q4=makeQuery(id+"F2.opExtrude","CAP_FACE",FACE,{"disambiguationData":[OSD([sQuery(id+"F0.wireOp",EDGE,"E12"),sQuery(id+"F0.wireOp",EDGE,"E13"),sQuery(id+"F0.wireOp",EDGE,"E14"),sQuery(id+"F0.wireOp",EDGE,"E15"),sQuery(id+"F0.wireOp",EDGE,"E17.filletArc"),sQuery(id+"F0.wireOp",EDGE,"E18.filletArc"),sQuery(id+"F0.wireOp",EDGE,"E19.filletArc"),sQuery(id+"F0.wireOp",EDGE,"E20.filletArc"),sQuery(id+"F0.wireOp",EDGE,"E25.0"),sQuery(id+"F0.wireOp",EDGE,"E25.1"),sQuery(id+"F0.wireOp",EDGE,"E25.2"),sQuery(id+"F0.wireOp",EDGE,"E25.3"),sQuery(id+"F0.wireOp",EDGE,"E25.4"),sQuery(id+"F0.wireOp",EDGE,"E25.5"),sQuery(id+"F0.wireOp",EDGE,"E25.6"),sQuery(id+"F0.wireOp",EDGE,"E25.7")])],"isStart":false});
            extrude(context, id + "F17", {"entities" : qUnion([Q0, Q1, Q2, Q3]), "operationType" : NewBodyOperationType.ADD, "endBound" : BoundingType.UP_TO_SURFACE, "endBoundEntityFace" : qUnion([Q4]), "depth" : 25 * mm});
        }
    });
